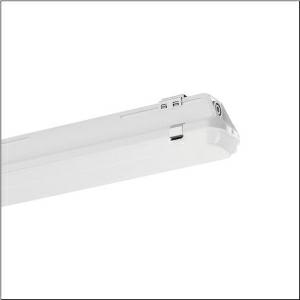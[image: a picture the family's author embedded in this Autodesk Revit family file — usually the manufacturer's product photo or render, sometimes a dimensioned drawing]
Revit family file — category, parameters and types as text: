
# Revit family: monsun_r__12_51fp20dp4b0q_e624
name_source: partatom
category: Lighting Fixtures
units: mm (PartAtom-declared; Revit-internal decimal feet)

## family parameters
Cut with Voids When Loaded = No
Host = Face
Light Source = No
Part Type = Normal
Room Calculation Point = No
Round Connector Dimension = Use Diameter
Shared = No

## types (1)
- --- (1 x LED, 10950 lm, 67.6 W, 4000K)
    Apparent Load = 68 VA
    CIE Flux Codes = 45 75 93 94 100
    Color Rendering = 80
    Color Temperature = 4000K
    Default Elevation = 1800 mm
    Description = Monsun® 12, damp-proof luminaire, chain hanger, primary optical cover: enclosure, of PC, light emission: direct distribution, primary light characteristic: symmetric, installation type: suspended mounting, surface-mounted, horizontal mounting, vertical mounting, LED rated luminous flux: 10.950 lm, light colour: 840, colour temperature: 4000K, control gear: ECG DALI, with terminal, 5-pole, max. 2.5mm², mains connection: 220..240V, AC, 50/60Hz, rated input power: 68W, luminaire housing, of glass-fibre reinforced polyester, uncoated, bright grey, length: 1.590 mm, width: 90 mm, height: 88mm, clip for enclosure, of stainless steel (V2A), ceiling mounting element, of stainless steel (V2A), chain hanger, of stainless steel (V2A), protection rating (complete): IP66, insulation class (complete): insulation class I (protective earthing), certification: CE, ENEC, VDE, protection symbol: D, impact resistance: IK08, permissible ambient temperature for indoor applications: -40..+35°C, standard: EN 50419, EN 60598-2-1, no direct snow, no direct sun, no direct rain, for indoor or canopied outdoor use, corresponds to IFS (International Featured Standards) requirements for safety and quality in the food industry, packaging unit: 1 piece
    Height = 89 mm
    Lamp = 1 x LED
    Lamp Light Flux = 10950 lm
    Lamp Power = 67.6 W
    Lamp count = 1
    Length = 1590 mm
    Luminous efficacy = 162 lm/W
    Manufacturer = Siteco
    ModVariant = No
    Model = 51FP20DP4B0Q
    Mounting Place = Ceiling
    Mounting Type = Pendant
    Number of Poles = 1
    OnlyDefault = Yes
    Power Factor = 1
    Product Name = Monsun® 12
    Product group = damp-proof luminaire | ceiling pendant
    ProductGroupID = 908
    Protection Class = Protection class I
    Protection Degree = IP 66
    RLX_Detail_Level = 1
    RlxData = <blob elided: 92005 chars, md5=586234f8>
    Socket = socket
    Standby Power = 0 W
    System Light Flux = 10950 lm
    System Power = 68 W
    Type Comments = factory setting: luminous flux: 100 % | dim-lin: 254 | 389 mA
    Type Image = l_1004748.jpg
    URL = http://relux.com
    VarID = @adj_133819
    Voltage = 0 V
    Weight = 0.00 kg
    Width = 90 mm

## geometry (parser evidence)
native form markers: Blend x4, Sweep x14
no freeform markers — native parametric forms only
